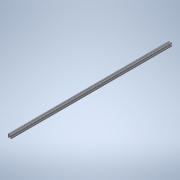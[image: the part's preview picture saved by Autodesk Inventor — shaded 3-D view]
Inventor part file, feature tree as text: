
AUTODESK INVENTOR PART (.ipt)
format: ipt  version: 2020 (Build 240168000, 168)  size: 208,384 bytes
history: native  units: in
note: dims shown in document units (in); Inventor stores cm internally (conversion verified against a paired STEP export)
features: extrude x1, sketch x1
ambient origin geometry x8: Origin, YZ Plane, XZ Plane, XY Plane, X Axis, Y Axis, Z Axis, Center Point
bodies: Solid1 (feature_tree)
feature tree (2):
  extrude  "Extrusion1"  [1 undecoded]
  sketch  "Sketch_1"  dims[d0=48.0in d1=0.0in]
note: 1 required parameter value undecoded (feature->parameter linkage not recoverable at this tier; creation-order binding heuristic only, values carry confidence <= 0.55)
